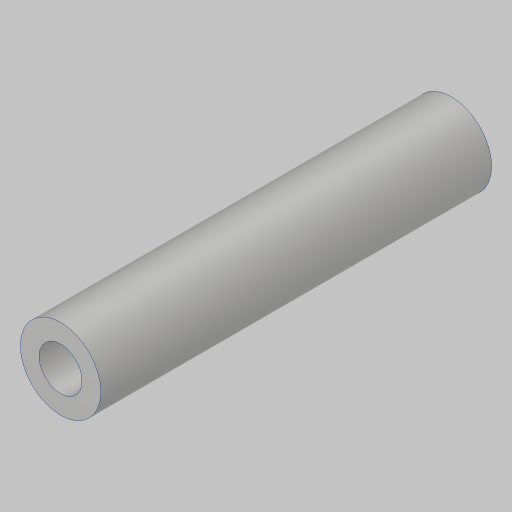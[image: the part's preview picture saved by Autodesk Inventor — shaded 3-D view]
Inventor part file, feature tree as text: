
AUTODESK INVENTOR PART (.ipt)
format: ipt  version: 2023.5 (Build 275446000, 446)  size: 108,032 bytes
history: native  units: in
note: dims shown in document units (in); Inventor stores cm internally (conversion verified against a paired STEP export)
features: extrude x1, hole x1
ambient origin geometry x8: Origin, YZ Plane, XZ Plane, XY Plane, X Axis, Y Axis, Z Axis, Center Point
bodies: Solid1 (feature_tree)
feature tree (2):
  extrude  "Extrusion1"  Depth=1.82in
  hole  "Hole1"  [1 undecoded]
note: 1 required parameter value undecoded (feature->parameter linkage not recoverable at this tier; creation-order binding heuristic only, values carry confidence <= 0.55)
